FCSTD DOCUMENT
Label: axihaum-modif-guides_fixes
objects: Part::Extrusion×28, Part::Part2DObjectPython×24, Part::Cut×22, PartDesign::Pocket×10, Part::Feature×9, Part::MultiFuse×7, App::DocumentObjectGroup×5, Part::Box×4, Part::Cylinder×3, PartDesign::Pad×2, Part::MultiCommon×1
note: 122 computed .brp shape members not serialized (recipe doc carries the construction recipe); baked Part::Feature solids carry a one-line shape summary decoded from their .brp

FEATURE [Part::Extrusion] Extrude
  Dir = (0,0,11.7)
  Solid = true
FEATURE [Part::Part2DObjectPython] Circle003  # Draft 2D object (typed FeaturePython)
  FirstAngle = 0
  LastAngle = 0
  Placement = pos=(48,12,0) rot=(0,0,1;0rad)
  Radius = 8
FEATURE [Part::Part2DObjectPython] Circle  # Draft 2D object (typed FeaturePython)
  FirstAngle = 0
  LastAngle = 0
  Placement = pos=(48,90,0) rot=(0,0,1;0rad)
  Radius = 8
FEATURE [Part::Part2DObjectPython] Circle004  # Draft 2D object (typed FeaturePython)
  FirstAngle = 0
  LastAngle = 0
  Placement = pos=(48,51,0) rot=(0,0,1;0rad)
  Radius = 4
FEATURE [Part::Extrusion] Extrude001
  Base = -> Circle003
  Dir = (0,0,11.7)
  Solid = false
FEATURE [Part::Extrusion] Extrude002
  Base = -> Circle
  Dir = (0,0,11.7)
  Solid = false
FEATURE [Part::Extrusion] Extrude003
  Base = -> Circle004
  Dir = (0,0,11.7)
  Solid = false
FEATURE [Part::Cut] Cut
  Base = -> Extrude
  Tool = -> Extrude001
FEATURE [Part::Cut] Cut001
  Base = -> Cut
  Tool = -> Extrude003
FEATURE [Part::Cut] Cut002  label="Y_P_L"
  Base = -> Cut001
  Placement = pos=(408.761,285.4,118.2) rot=(0,0.707107,0.707107;3.14159rad)
  Tool = -> Extrude002
FEATURE [Part::Part2DObjectPython] Circle008  # Draft 2D object (typed FeaturePython)
  FirstAngle = 0
  LastAngle = 0
  Placement = pos=(48,90,0) rot=(0,0,1;0rad)
  Radius = 8
FEATURE [Part::Extrusion] Extrude004  label="Y_G_U"
  Base = -> Circle008
  Dir = (0,0,355)
  Placement = pos=(408.761,-57.9,118.2) rot=(0,0.707107,0.707107;3.14159rad)
  Solid = true
FEATURE [Part::Part2DObjectPython] Circle009  # Draft 2D object (typed FeaturePython)
  FirstAngle = 0
  LastAngle = 0
  Placement = pos=(48,12,0) rot=(0,0,1;0rad)
  Radius = 8
FEATURE [Part::Extrusion] Extrude005  label="Y_G_D"
  Base = -> Circle009
  Dir = (0,0,355)
  Placement = pos=(408.761,-57.9,118.2) rot=(0,0.707107,0.707107;3.14159rad)
  Solid = true
FEATURE [Part::Part2DObjectPython] Circle013  # Draft 2D object (typed FeaturePython)
  FirstAngle = 0
  LastAngle = 0
  Placement = pos=(48,51,0) rot=(0,0,1;0rad)
  Radius = 20
FEATURE [Part::Part2DObjectPython] Circle014  # Draft 2D object (typed FeaturePython)
  FirstAngle = 0
  LastAngle = 0
  Placement = pos=(48,90,0) rot=(0,0,1;0rad)
  Radius = 8
FEATURE [Part::Part2DObjectPython] Circle015  # Draft 2D object (typed FeaturePython)
  FirstAngle = 0
  LastAngle = 0
  Placement = pos=(48,12,0) rot=(0,0,1;0rad)
  Radius = 8
FEATURE [Part::Extrusion] Extrude006
  Base = -> Circle013
  Dir = (0,0,11.7)
  Solid = true
FEATURE [Part::Feature] Face
  shape: bbox 90 x 120 x 2e-07 mm, 1 faces, 0 solids (baked)
FEATURE [Part::Extrusion] Extrude007
  Base = -> Circle014
  Dir = (0,0,11.7)
  Solid = true
FEATURE [Part::Extrusion] Extrude008
  Base = -> Circle015
  Dir = (0,0,11.7)
  Solid = true
FEATURE [Part::Extrusion] Extrude009
  Base = -> Face
  Dir = (0,0,11.7)
  Solid = true
FEATURE [Part::Cut] Cut003
  Base = -> Extrude009
  Tool = -> Extrude008
FEATURE [Part::Cut] Cut004
  Base = -> Cut003
  Tool = -> Extrude007
FEATURE [Part::Cut] Cut005  label="Y_P_R"
  Base = -> Cut004
  Placement = pos=(408.761,-57.5,118.2) rot=(0,0.707107,0.707107;3.14159rad)
  Tool = -> Extrude006
FEATURE [Part::Cylinder] Cylinder  label="Y_SC"
  Angle = 360
  Height = 10
  Placement = pos=(360.651,-52.9,169.2) rot=(0.57735,0.57735,0.57735;4.18879rad)
  Radius = 10
FEATURE [Part::Cylinder] Cylinder001  label="Y_S"
  Angle = 360
  Height = 335
  Placement = pos=(360.651,-47.9,169.2) rot=(-0.57735,-0.57735,-0.57735;2.0944rad)
  Radius = 5.6
FEATURE [Part::Feature] Face001
  shape: bbox 100 x 55 x 2e-07 mm, 1 faces, 0 solids (baked)
FEATURE [Part::Part2DObjectPython] Circle024  # Draft 2D object (typed FeaturePython)
  FirstAngle = 0
  LastAngle = 0
  Placement = pos=(12,7,0) rot=(0,0,1;0rad)
  Radius = 3
FEATURE [Part::Part2DObjectPython] Circle025  # Draft 2D object (typed FeaturePython)
  FirstAngle = 0
  LastAngle = 0
  Placement = pos=(88,7,0) rot=(0,0,1;0rad)
  Radius = 3
FEATURE [Part::Part2DObjectPython] Circle026  # Draft 2D object (typed FeaturePython)
  FirstAngle = 0
  LastAngle = 0
  Placement = pos=(12,48,0) rot=(0,0,1;0rad)
  Radius = 3
FEATURE [Part::Part2DObjectPython] Circle027  # Draft 2D object (typed FeaturePython)
  FirstAngle = 0
  LastAngle = 0
  Placement = pos=(88,48,0) rot=(0,0,1;0rad)
  Radius = 3
FEATURE [Part::Extrusion] Extrude010
  Base = -> Face001
  Dir = (0,0,11.7)
  Solid = false
FEATURE [Part::Extrusion] Extrude011
  Base = -> Circle024
  Dir = (0,0,11.7)
  Solid = false
FEATURE [Part::Extrusion] Extrude013
  Base = -> Circle026
  Dir = (0,0,11.7)
  Solid = false
FEATURE [Part::Extrusion] Extrude012
  Base = -> Circle025
  Dir = (0,0,11.7)
  Solid = false
FEATURE [Part::Extrusion] Extrude014
  Base = -> Circle027
  Dir = (0,0,11.7)
  Solid = false
FEATURE [Part::Cut] Cut006
  Base = -> Extrude010
  Tool = -> Extrude011
FEATURE [Part::Cut] Cut007
  Base = -> Cut006
  Tool = -> Extrude014
FEATURE [Part::Cut] Cut008
  Base = -> Cut007
  Tool = -> Extrude012
FEATURE [Part::Cut] Cut009
  Base = -> Cut008
  Tool = -> Extrude013
FEATURE [Part::Part2DObjectPython] Circle028  # Draft 2D object (typed FeaturePython)
  FirstAngle = 0
  LastAngle = 0
  Placement = pos=(12,48,0) rot=(0,0,1;0rad)
  Radius = 6
FEATURE [Part::Part2DObjectPython] Circle029  # Draft 2D object (typed FeaturePython)
  FirstAngle = 0
  LastAngle = 0
  Placement = pos=(88,48,0) rot=(0,0,1;0rad)
  Radius = 6
FEATURE [Part::Extrusion] Extrude015
  Base = -> Circle028
  Dir = (0,0,6)
  Solid = false
FEATURE [Part::Extrusion] Extrude016
  Base = -> Circle029
  Dir = (0,0,6)
  Solid = false
FEATURE [Part::Cut] Cut010
  Base = -> Cut009
  Tool = -> Extrude015
FEATURE [Part::Cut] Cut011
  Base = -> Cut010
  Tool = -> Extrude016
FEATURE [Part::Part2DObjectPython] Circle030  # Draft 2D object (typed FeaturePython)
  FirstAngle = 0
  LastAngle = 0
  Placement = pos=(88,7,0) rot=(0,0,1;0rad)
  Radius = 6
FEATURE [Part::Part2DObjectPython] Circle031  # Draft 2D object (typed FeaturePython)
  FirstAngle = 0
  LastAngle = 0
  Placement = pos=(12,7,0) rot=(0,0,1;0rad)
  Radius = 6
FEATURE [Part::Extrusion] Extrude017
  Base = -> Circle030
  Dir = (0,0,6.5)
  Placement = pos=(0,0,5.2) rot=(0,0,1;0rad)
  Solid = false
FEATURE [Part::Extrusion] Extrude018
  Base = -> Circle031
  Dir = (0,0,6.5)
  Placement = pos=(0,0,5.2) rot=(0,0,1;0rad)
  Solid = false
FEATURE [Part::Cut] Cut012
  Base = -> Cut011
  Tool = -> Extrude017
FEATURE [Part::Cut] Cut013  label="X_SY_RT"
  Base = -> Cut012
  Placement = pos=(440.2,-2.5,-11.8) rot=(0,0,1;3.14159rad)
  Tool = -> Extrude018
FEATURE [Part::Feature] Cut014  label="X_SY_LT"
  Placement = pos=(339.999,242.3,-11.7) rot=(0,0,1;0rad)
  shape: bbox 100 x 55 x 11.7 mm, 18 faces (baked)
FEATURE [Part::Feature] Face004
  shape: bbox 100 x 268 x 2e-07 mm, 1 faces, 0 solids (baked)
FEATURE [Part::Part2DObjectPython] Circle056  # Draft 2D object (typed FeaturePython)
  FirstAngle = 0
  LastAngle = 0
  Placement = pos=(12,7,0) rot=(0,0,1;0rad)
  Radius = 6
FEATURE [Part::Part2DObjectPython] Circle057  # Draft 2D object (typed FeaturePython)
  FirstAngle = 0
  LastAngle = 0
  Placement = pos=(88,261,0) rot=(0,0,1;0rad)
  Radius = 6
FEATURE [Part::Part2DObjectPython] Circle058  # Draft 2D object (typed FeaturePython)
  FirstAngle = 0
  LastAngle = 0
  Placement = pos=(12,261,0) rot=(0,0,1;0rad)
  Radius = 6
FEATURE [Part::Part2DObjectPython] Circle059  # Draft 2D object (typed FeaturePython)
  FirstAngle = 0
  LastAngle = 0
  Placement = pos=(88,7,0) rot=(0,0,1;0rad)
  Radius = 6
FEATURE [Part::Extrusion] Extrude029
  Base = -> Face004
  Dir = (0,0,-8.1)
  Solid = true
FEATURE [Part::Extrusion] Extrude030
  Base = -> Circle056
  Dir = (0,0,-4.2)
  Solid = true
FEATURE [Part::Extrusion] Extrude031
  Base = -> Circle057
  Dir = (0,0,-4.2)
  Solid = true
FEATURE [Part::Extrusion] Extrude032
  Base = -> Circle058
  Dir = (0,0,-4.2)
  Solid = true
FEATURE [Part::Extrusion] Extrude033
  Base = -> Circle059
  Dir = (0,0,-4.2)
  Solid = true
FEATURE [Part::Cut] Cut023
  Base = -> Extrude029
  Tool = -> Extrude033
FEATURE [Part::Cut] Cut024
  Base = -> Cut023
  Tool = -> Extrude030
FEATURE [Part::Cut] Cut025
  Base = -> Cut024
  Tool = -> Extrude032
FEATURE [Part::Cut] Cut026
  Base = -> Cut025
  Tool = -> Extrude031
FEATURE [Part::Part2DObjectPython] Circle060  # Draft 2D object (typed FeaturePython)
  FirstAngle = 0
  LastAngle = 0
  Placement = pos=(12,7,0) rot=(0,0,1;0rad)
  Radius = 3
FEATURE [Part::Part2DObjectPython] Circle061  # Draft 2D object (typed FeaturePython)
  FirstAngle = 0
  LastAngle = 0
  Placement = pos=(88,7,0) rot=(0,0,1;0rad)
  Radius = 3
FEATURE [Part::Part2DObjectPython] Circle062  # Draft 2D object (typed FeaturePython)
  FirstAngle = 0
  LastAngle = 0
  Placement = pos=(88,261,0) rot=(0,0,1;0rad)
  Radius = 3
FEATURE [Part::Part2DObjectPython] Circle063  # Draft 2D object (typed FeaturePython)
  FirstAngle = 0
  LastAngle = 0
  Placement = pos=(12,261,0) rot=(0,0,1;0rad)
  Radius = 3
FEATURE [Part::Extrusion] Extrude034
  Base = -> Circle063
  Dir = (0,0,-8.1)
  Solid = true
FEATURE [Part::Extrusion] Extrude035
  Base = -> Circle060
  Dir = (0,0,-8.1)
  Solid = true
FEATURE [Part::Extrusion] Extrude036
  Base = -> Circle061
  Dir = (0,0,-8.1)
  Solid = true
FEATURE [Part::Extrusion] Extrude037
  Base = -> Circle062
  Dir = (0,0,-8.1)
  Solid = true
FEATURE [Part::Cut] Cut027
  Base = -> Cut026
  Tool = -> Extrude034
FEATURE [Part::Cut] Cut028
  Base = -> Cut027
  Tool = -> Extrude037
FEATURE [Part::Cut] Cut029
  Base = -> Cut028
  Tool = -> Extrude036
FEATURE [Part::Cut] Cut030  label="X_SY_B"
  Base = -> Cut029
  Placement = pos=(461.639,-14,-62.9) rot=(0,1,0;3.14159rad)
  Tool = -> Extrude035
FEATURE [PartDesign::Pocket] Pocket  label="C_T"
  Length = 5
  Placement = pos=(500,240,-14.7) rot=(0,0,1;3.14159rad)
  Type = 0
FEATURE [Part::Box] Box001  label="C_B"
  Height = 125
  Length = 11.7
  Placement = pos=(489.999,240,-139.7) rot=(0,0,1;3.14159rad)
  Width = 240
FEATURE [Part::Box] Box001001  label="C_F"
  Height = 125
  Length = 11.7
  Placement = pos=(11.7,240,-139.7) rot=(0,0,1;3.14159rad)
  Width = 240
FEATURE [Part::Box] Box  label="X Axis"
  Height = 38
  Length = 466
  Placement = pos=(478.299,240,-52.7) rot=(0,0,1;3.14159rad)
  Width = 240
FEATURE [PartDesign::Pocket] Pocket001  label="Z_P"
  Length = 5
  Placement = pos=(385.261,14.8,102.2) rot=(0.57735,0.57735,0.57735;2.0944rad)
  Type = 1
FEATURE [PartDesign::Pocket] Pocket002  label="A_LB_Y0_alu"
  Length = 5
  Placement = pos=(385.261,72.8,158.2) rot=(0.707107,0,-0.707107;3.14159rad)
  Type = 1
FEATURE [PartDesign::Pocket] Pocket003  label="A_LB_Y0_plastic"
  Length = 5
  Placement = pos=(385.261,72.8,158.2) rot=(0.707107,0,-0.707107;3.14159rad)
  Type = 1
FEATURE [PartDesign::Pocket] Pocket004  label="A_LB_Y1_plastic"
  Length = 5
  Placement = pos=(385.261,110.8,236.2) rot=(0.707107,0,-0.707107;3.14159rad)
  Type = 1
FEATURE [PartDesign::Pocket] Pocket005  label="A_LB_Y1_alu"
  Length = 5
  Placement = pos=(385.261,110.8,236.2) rot=(0.707107,0,-0.707107;3.14159rad)
  Type = 1
FEATURE [PartDesign::Pocket] Pocket006  label="A_LB_Y2_plastic"
  Length = 5
  Placement = pos=(385.261,32.8,236.2) rot=(0.707107,0,-0.707107;3.14159rad)
  Type = 1
FEATURE [PartDesign::Pocket] Pocket007  label="A_LB_Y2_alu"
  Length = 5
  Placement = pos=(385.261,32.8,236.2) rot=(0.707107,0,-0.707107;3.14159rad)
  Type = 1
FEATURE [App::DocumentObjectGroup] Groupe002  label="Case"
  Group = -> [Pocket,Box001,Box001001,Box]
FEATURE [App::DocumentObjectGroup] Groupe004  label="Linear Bearings"
  Group = -> [Pocket002,Pocket003,Pocket004,Pocket005,Pocket006,Pocket007]
FEATURE [Part::Box] Box001002  label="Box001"
  Height = 200
  Length = 10
  Placement = pos=(451.499,15,121) rot=(0,0,1;0rad)
  Width = 120
FEATURE [Part::MultiFuse] Fusion  label="Z_B"
  Placement = pos=(390.261,14.8,102.2) rot=(0,0,1;0rad)
FEATURE [Part::MultiCommon] Common
  Placement = pos=(506,75,175) rot=(0,0,1;0rad)
FEATURE [Part::MultiFuse] Fusion001
  Placement = pos=(0,0,1) rot=(0,0,1;0rad)
  Shapes = -> [Box001002,Common]
FEATURE [Part::Feature] Pocket009  label="SBR12UU001"
  Placement = pos=(423.499,56,322) rot=(0,0,-1;1.5708rad)
  shape: bbox 28 x 41 x 39 mm, 18 faces (baked)
FEATURE [Part::Feature] Pocket010  label="SBR12UU002"
  Placement = pos=(423.499,56,222) rot=(0,0,-1;1.5708rad)
  shape: bbox 28 x 41 x 39 mm, 18 faces (baked)
FEATURE [Part::Feature] Pocket011  label="SBR12UU003"
  Placement = pos=(423.499,135,322) rot=(0,0,-1;1.5708rad)
  shape: bbox 28 x 41 x 39 mm, 18 faces (baked)
FEATURE [Part::Feature] Pocket012  label="SBR12UU004"
  Placement = pos=(423.499,135,222) rot=(0,0,-1;1.5708rad)
  shape: bbox 28 x 41 x 39 mm, 18 faces (baked)
FEATURE [Part::Cylinder] Cylinder002  label="Z_G_L"
  Angle = 360
  Height = 250
  Placement = pos=(412.761,35.3,102.2) rot=(0,0,1;0rad)
  Radius = 6
FEATURE [Part::Feature] Cylinder003  label="Z_G_R"
  Placement = pos=(412.761,114.3,111.2) rot=(0,0,1;0rad)
  shape: bbox 12 x 12 x 250 mm, 3 faces (baked)
FEATURE [Part::MultiFuse] Fusion002
  Shapes = -> [Pocket010,Pocket009]
FEATURE [Part::MultiFuse] Fusion003  label="Fusion007"
  Shapes = -> [Pocket012,Pocket011]
FEATURE [Part::MultiFuse] Fusion004  label="Fusion008"
  Shapes = -> [Fusion002,Fusion003]
FEATURE [Part::MultiFuse] Fusion005  label="Z_F_spindle"
  Placement = pos=(-21.238,-0.2,-72) rot=(0,0,1;0rad)
  Shapes = -> [Fusion001,Fusion004]
FEATURE [App::DocumentObjectGroup] Groupe003  label="Z Axis"
  Group = -> [Pocket001,Fusion,Cylinder002,Cylinder003,Fusion005]
FEATURE [PartDesign::Pad] Pad  label="X_SY_M"
  Length = 11.5
  Length2 = 100
  Placement = pos=(361.639,-2.5,-54.8) rot=(1,0,0;1.5708rad)
  Type = 0
FEATURE [App::DocumentObjectGroup] Groupe001  label="X_SY"
  Group = -> [Cut013,Cut014,Cut030,Pad]
FEATURE [PartDesign::Pad] Pad001  label="Y_SZ_L"
  Length = 10
  Length2 = 100
  Placement = pos=(340.2,-57.5,-11.8) rot=(1,0,0;1.5708rad)
  Type = 0
FEATURE [App::DocumentObjectGroup] Groupe  label="Y Axis"
  Group = -> [Cut002,Extrude004,Extrude005,Cut005,Cylinder,Cylinder001,Groupe004,Pad001]
FEATURE [PartDesign::Pocket] Pocket013  label="Z_C"
  Length = 23
  Placement = pos=(419.761,74.8,325.7) rot=(0,0,1;0rad)
  Type = 0
FEATURE [PartDesign::Pocket] Pocket014  label="Z_T_SB_T"
  Length = 5
  Placement = pos=(400.261,59.8,307.2) rot=(0,0,1;0rad)
  Type = 1
FEATURE [Part::MultiFuse] Fusion006  label="Z_T"
  Placement = pos=(409.261,58.8,280) rot=(0,1,0;1.5708rad)
